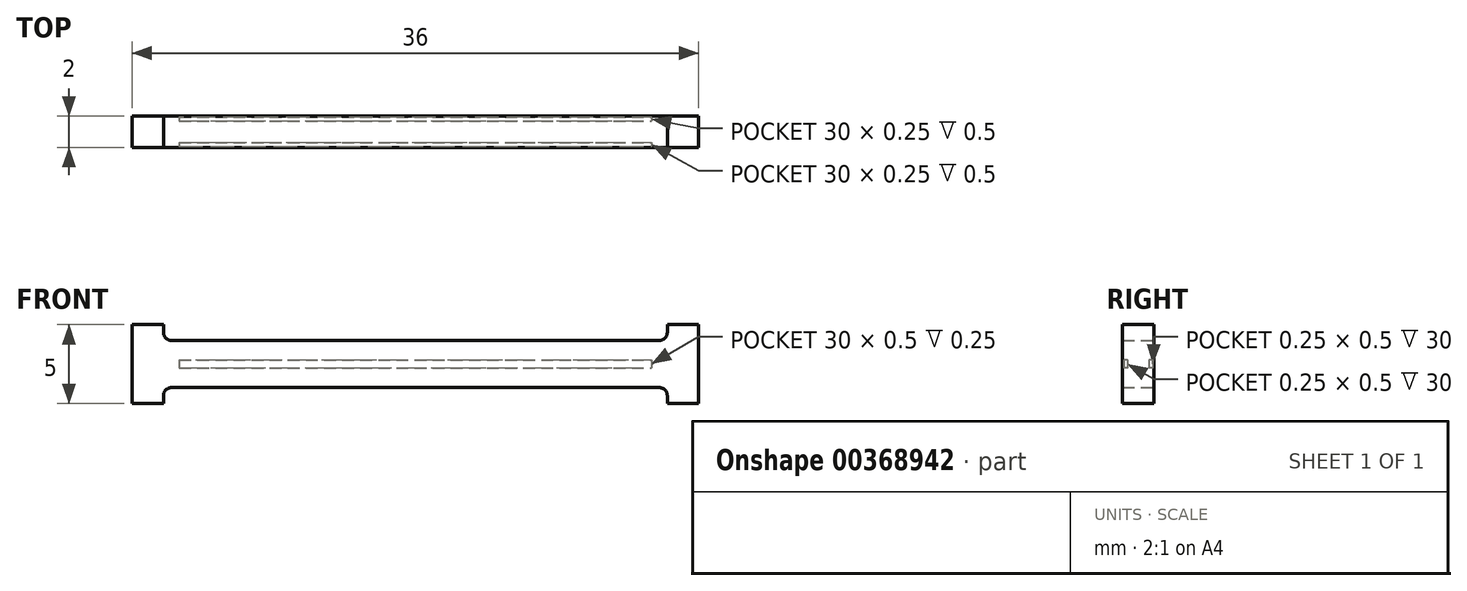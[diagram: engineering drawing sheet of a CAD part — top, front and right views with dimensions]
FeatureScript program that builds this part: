
annotation { "Feature Type Name" : "Feature", "Feature Type Description" : "" }
export const myFeature = defineFeature(function(context is Context, id is Id, definition is map)
    precondition{}
    {
        {
            var Q0;
            Q0=qCreatedBy(makeId("Front.planeOp"),FACE);
            var sketch = newSketch(context, id + "F0", { "sketchPlane" : qUnion([Q0])});
            skLineSegment(sketch, "E0", {"start": v(-18, 2.5) * mm, "end": v(-18, 0) * mm});
            skLineSegment(sketch, "E1", {"start": v(-18, 2.5) * mm, "end": v(-16, 2.5) * mm});
            skLineSegment(sketch, "E2", {"start": v(0, 0) * mm, "end": v(0, 3.35) * mm});
            skLineSegment(sketch, "E3", {"start": v(-18, 0) * mm, "end": v(18, 0) * mm});
            skLineSegment(sketch, "E4", {"start": v(-16, 2.5) * mm, "end": v(-16, 2) * mm});
            skLineSegment(sketch, "E5", {"start": v(-15.5, 1.5) * mm, "end": v(0, 1.5) * mm});
            skPoint(sketch, "E6.visualSharp", {"position": v(-16, 1.5) * mm});
            skArc(sketch, "E6.filletArc", {"start": v(-16, 2) * mm, "mid": v(-15.85, 1.65) * mm, "end": v(-15.5, 1.5) * mm});
            skLineSegment(sketch, "E7.MirrorCS", {"start": v(15.5, 1.5) * mm, "end": v(0, 1.5) * mm});
            skArc(sketch, "E8.MirrorCS", {"start": v(16, 2) * mm, "mid": v(15.85, 1.65) * mm, "end": v(15.5, 1.5) * mm});
            skLineSegment(sketch, "E9.MirrorCS", {"start": v(16, 2.5) * mm, "end": v(16, 2) * mm});
            skLineSegment(sketch, "E10.MirrorCS", {"start": v(18, 2.5) * mm, "end": v(16, 2.5) * mm});
            skLineSegment(sketch, "E11.MirrorCS", {"start": v(18, 2.5) * mm, "end": v(18, 0) * mm});
            skLineSegment(sketch, "E12.MirrorCS", {"start": v(-18, -2.5) * mm, "end": v(-18, 0) * mm});
            skLineSegment(sketch, "E13.MirrorCS", {"start": v(-18, -2.5) * mm, "end": v(-16, -2.5) * mm});
            skLineSegment(sketch, "E14.MirrorCS", {"start": v(-16, -2.5) * mm, "end": v(-16, -2) * mm});
            skArc(sketch, "E15.MirrorCS", {"start": v(-16, -2) * mm, "mid": v(-15.85, -1.65) * mm, "end": v(-15.5, -1.5) * mm});
            skLineSegment(sketch, "E16.MirrorCS", {"start": v(-15.5, -1.5) * mm, "end": v(0, -1.5) * mm});
            skLineSegment(sketch, "E17.MirrorCS", {"start": v(15.5, -1.5) * mm, "end": v(0, -1.5) * mm});
            skArc(sketch, "E18.MirrorCS", {"start": v(16, -2) * mm, "mid": v(15.85, -1.65) * mm, "end": v(15.5, -1.5) * mm});
            skLineSegment(sketch, "E19.MirrorCS", {"start": v(16, -2.5) * mm, "end": v(16, -2) * mm});
            skLineSegment(sketch, "E20.MirrorCS", {"start": v(18, -2.5) * mm, "end": v(16, -2.5) * mm});
            skLineSegment(sketch, "E21.MirrorCS", {"start": v(18, -2.5) * mm, "end": v(18, 0) * mm});
            skSolve(sketch);
        }
        {
            var Q0;
            {var subQ1=sQuery(id+"F0.wireOp",EDGE,"E0");Q0=makeQuery(id+"F0.imprint","IMPRINT",FACE,{"disambiguationData":[TD([[makeQuery(id+"F0.imprint","IMPRINT",EDGE,{"derivedFrom":subQ1}),1.0]])]});}
            var Q1;
            {var subQ0=sQuery(id+"F0.wireOp",EDGE,"E7.MirrorCS");Q1=makeQuery(id+"F0.imprint","IMPRINT",FACE,{"disambiguationData":[TD([[makeQuery(id+"F0.imprint","IMPRINT",EDGE,{"derivedFrom":subQ0}),1.0]])]});}
            var Q2;
            {var subQ0=sQuery(id+"F0.wireOp",EDGE,"E12.MirrorCS");Q2=makeQuery(id+"F0.imprint","IMPRINT",FACE,{"disambiguationData":[TD([[makeQuery(id+"F0.imprint","IMPRINT",EDGE,{"derivedFrom":subQ0}),-1.0]])]});}
            extrude(context, id + "F1", {"entities" : qUnion([Q0, Q1, Q2]), "endBound" : BoundingType.SYMMETRIC, "depth" : 2 * mm});
        }
        {
            var Q0;
            Q0=qCreatedBy(makeId("Right.planeOp"),FACE);
            cPlane(context, id + "F2", {"entities" : qUnion([Q0]), "cplaneType" : CPlaneType.OFFSET, "offset" : 15 * mm, "width" : 150 * mm, "height" : 150 * mm});
        }
        {
            var Q0;
            Q0=qCreatedBy(id+"F2.planeOp",FACE);
            var sketch = newSketch(context, id + "F3", { "sketchPlane" : qUnion([Q0])});
            skPoint(sketch, "E22.middle", {"position": v(0, 0) * mm});
            skPoint(sketch, "E23", {"position": v(0.8, 0) * mm});
            skLineSegment(sketch, "E24.bottom", {"start": v(0.93, 0.25) * mm, "end": v(0.67, 0.25) * mm});
            skLineSegment(sketch, "E24.top", {"start": v(0.93, -0.25) * mm, "end": v(0.67, -0.25) * mm});
            skLineSegment(sketch, "E24.left", {"start": v(0.93, 0.25) * mm, "end": v(0.93, -0.25) * mm});
            skLineSegment(sketch, "E24.right", {"start": v(0.67, 0.25) * mm, "end": v(0.67, -0.25) * mm});
            skPoint(sketch, "E25", {"position": v(-0.8, 0) * mm});
            skLineSegment(sketch, "E26.bottom", {"start": v(-0.68, 0.25) * mm, "end": v(-0.93, 0.25) * mm});
            skLineSegment(sketch, "E26.top", {"start": v(-0.68, -0.25) * mm, "end": v(-0.93, -0.25) * mm});
            skLineSegment(sketch, "E26.left", {"start": v(-0.68, 0.25) * mm, "end": v(-0.68, -0.25) * mm});
            skLineSegment(sketch, "E26.right", {"start": v(-0.93, 0.25) * mm, "end": v(-0.93, -0.25) * mm});
            skLineSegment(sketch, "E27", {"start": v(0, 0) * mm, "end": v(0.8, 0) * mm});
            skLineSegment(sketch, "E28.MirrorCS", {"start": v(0, 0) * mm, "end": v(-0.8, 0) * mm});
            skSolve(sketch);
        }
        {
            var Q0;
            {var subQ3=sQuery(id+"F3.wireOp",EDGE,"E26.bottom");Q0=makeQuery(id+"F3.imprint","IMPRINT",FACE,{"disambiguationData":[TD([[makeQuery(id+"F3.imprint","IMPRINT",EDGE,{"derivedFrom":subQ3}),1.0]])]});}
            var Q1;
            {var subQ1=sQuery(id+"F3.wireOp",EDGE,"E24.bottom");Q1=makeQuery(id+"F3.imprint","IMPRINT",FACE,{"disambiguationData":[TD([[makeQuery(id+"F3.imprint","IMPRINT",EDGE,{"derivedFrom":subQ1}),1.0]])]});}
            extrude(context, id + "F4", {"entities" : qUnion([Q0, Q1]), "oppositeDirection" : true, "depth" : 30 * mm});
        }
        {
            var Q0;
            {var subQ1=sQuery(id+"F3.wireOp",EDGE,"E24.bottom");Q0=makeQuery(id+"F3.imprint","IMPRINT",FACE,{"disambiguationData":[TD([[makeQuery(id+"F3.imprint","IMPRINT",EDGE,{"derivedFrom":subQ1}),1.0]])]});}
            var Q1;
            {var subQ3=sQuery(id+"F3.wireOp",EDGE,"E26.bottom");Q1=makeQuery(id+"F3.imprint","IMPRINT",FACE,{"disambiguationData":[TD([[makeQuery(id+"F3.imprint","IMPRINT",EDGE,{"derivedFrom":subQ3}),1.0]])]});}
            extrude(context, id + "F5", {"entities" : qUnion([Q0, Q1]), "operationType" : NewBodyOperationType.REMOVE, "oppositeDirection" : true, "depth" : 30 * mm});
        }
    });
